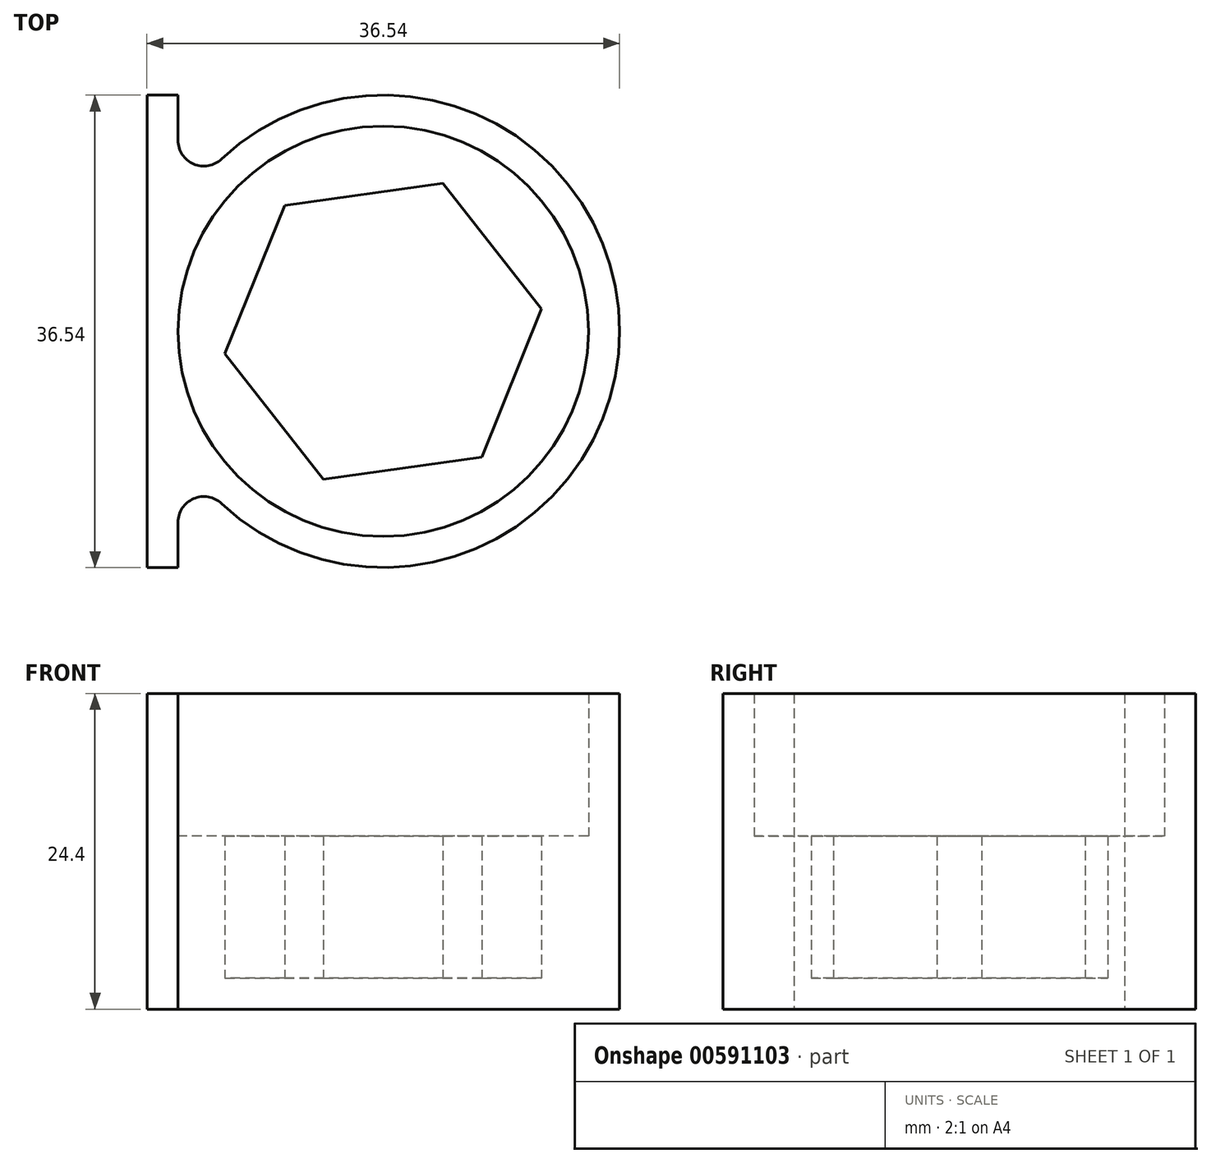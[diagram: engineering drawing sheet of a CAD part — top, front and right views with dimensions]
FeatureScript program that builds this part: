
annotation { "Feature Type Name" : "Feature", "Feature Type Description" : "" }
export const myFeature = defineFeature(function(context is Context, id is Id, definition is map)
    precondition{}
    {
        {
            assignVariable(context, id + "F0", {"name" : "WallThickness", "anyValue" : 2.4 * mm});
        }
        {
            assignVariable(context, id + "F1", {"name" : "HexHeight", "anyValue" : 11 * mm});
        }
        {
            var Q0;
            Q0=qCreatedBy(makeId("Top.planeOp"),FACE);
            var sketch = newSketch(context, id + "F2", { "sketchPlane" : qUnion([Q0])});
            skCircle(sketch, "E0", {"center": v(0, 0) * mm, "radius": 15.86 * mm});
            skCircle(sketch, "E1.cCircle", {"center": v(0, 0) * mm, "radius": 10.7 * mm, "construction": true});
            skLineSegment(sketch, "E1.0", {"start": v(4.62, 11.46) * mm, "end": v(12.23, 1.73) * mm});
            skLineSegment(sketch, "E1.1", {"start": v(12.23, 1.73) * mm, "end": v(7.61, -9.73) * mm});
            skLineSegment(sketch, "E1.2", {"start": v(7.61, -9.73) * mm, "end": v(-4.62, -11.46) * mm});
            skLineSegment(sketch, "E1.3", {"start": v(-4.62, -11.46) * mm, "end": v(-12.23, -1.73) * mm});
            skLineSegment(sketch, "E1.4", {"start": v(-12.23, -1.73) * mm, "end": v(-7.61, 9.73) * mm});
            skLineSegment(sketch, "E1.5", {"start": v(-7.61, 9.73) * mm, "end": v(4.62, 11.46) * mm});
            skPoint(sketch, "E1.0.midPoint", {"position": v(8.43, 6.6) * mm});
            skCircle(sketch, "E2", {"center": v(0, 0) * mm, "radius": 18.26 * mm});
            skLineSegment(sketch, "E3", {"start": v(17.7, 18.27) * mm, "end": v(-22.17, 18.26) * mm, "construction": true});
            skLineSegment(sketch, "E4", {"start": v(-22.17, -18.26) * mm, "end": v(17.7, -18.26) * mm, "construction": true});
            skLineSegment(sketch, "E5", {"start": v(-15.87, 18.26) * mm, "end": v(-15.86, -18.26) * mm});
            skLineSegment(sketch, "E6", {"start": v(-18.27, 18.26) * mm, "end": v(-18.26, -18.26) * mm});
            skLineSegment(sketch, "E7", {"start": v(-18.27, 18.26) * mm, "end": v(-15.87, 18.26) * mm});
            skLineSegment(sketch, "E8", {"start": v(-18.26, -18.26) * mm, "end": v(-15.86, -18.26) * mm});
            skSolve(sketch);
        }
        {
            var Q0;
            {var subQ0=sQuery(id+"F2.wireOp",EDGE,"E2");var subQ1=makeQuery(id+"F2.imprint","INTERSECT",VERTEX,{"derivedFrom":[subQ0,sQuery(id+"F2.wireOp",EDGE,"E6")]});Q0=makeQuery(id+"F2.imprint","IMPRINT",FACE,{"disambiguationData":[TD([[makeQuery(id+"F2.imprint","IMPRINT",EDGE,{"disambiguationData":[TD([[subQ1,1.0]])],"derivedFrom":subQ0}),1.0]])]});}
            var Q1;
            {var subQ5=sQuery(id+"F2.wireOp",EDGE,"E7");Q1=makeQuery(id+"F2.imprint","IMPRINT",FACE,{"disambiguationData":[TD([[makeQuery(id+"F2.imprint","IMPRINT",EDGE,{"derivedFrom":subQ5}),-1.0]])]});}
            var Q2;
            {var subQ5=sQuery(id+"F2.wireOp",EDGE,"E8");Q2=makeQuery(id+"F2.imprint","IMPRINT",FACE,{"disambiguationData":[TD([[makeQuery(id+"F2.imprint","IMPRINT",EDGE,{"derivedFrom":subQ5}),1.0]])]});}
            var Q3;
            {var subQ0=sQuery(id+"F2.wireOp",EDGE,"E0");Q3=makeQuery(id+"F2.imprint","IMPRINT",FACE,{"disambiguationData":[TD([[makeQuery(id+"F2.imprint","IMPRINT",EDGE,{"derivedFrom":subQ0}),-1.0]])]});}
            extrude(context, id + "F3", {"entities" : qUnion([Q0, Q1, Q2, Q3]), "depth" : 22 * mm + getVariable(context, 'WallThickness'), "offsetDistance" : 25 * mm});
        }
        {
            var Q0;
            Q0=makeQuery(id+"F2.imprint","IMPRINT",FACE,{"disambiguationData":[TD([[makeQuery(id+"F2.imprint","IMPRINT",EDGE,{"derivedFrom":sQuery(id+"F2.wireOp",EDGE,"E1.0")}),-1.0]])]});
            var Q1;
            Q1=makeQuery(id+"F2.imprint","IMPRINT",FACE,{"disambiguationData":[TD([[makeQuery(id+"F2.imprint","IMPRINT",EDGE,{"derivedFrom":sQuery(id+"F2.wireOp",EDGE,"E0")}),1.0]])]});
            var Q2;
            {var subQ0=sQuery(id+"F2.wireOp",EDGE,"E0");Q2=makeQuery(id+"F2.imprint","IMPRINT",FACE,{"disambiguationData":[TD([[makeQuery(id+"F2.imprint","IMPRINT",EDGE,{"derivedFrom":subQ0}),-1.0]])]});}
            extrude(context, id + "F4", {"entities" : qUnion([Q0, Q1, Q2]), "operationType" : NewBodyOperationType.ADD, "depth" : getVariable(context, 'WallThickness'), "offsetDistance" : 25 * mm});
        }
        {
            var Q0;
            Q0=makeQuery(id+"F2.imprint","IMPRINT",FACE,{"disambiguationData":[TD([[makeQuery(id+"F2.imprint","IMPRINT",EDGE,{"derivedFrom":sQuery(id+"F2.wireOp",EDGE,"E0")}),1.0]])]});
            extrude(context, id + "F5", {"entities" : qUnion([Q0]), "operationType" : NewBodyOperationType.ADD, "depth" : getVariable(context, 'HexHeight') + getVariable(context, 'WallThickness'), "offsetDistance" : 25 * mm});
        }
        {
            var Q0;
            {var subQ0=sQuery(id+"F2.wireOp",EDGE,"E5");var subQ1=sQuery(id+"F2.wireOp",EDGE,"E2");Q0=makeQuery(id+"F3.opExtrude","SWEPT_EDGE",EDGE,{"disambiguationData":[OSD([subQ1,subQ0]),TDD([makeQuery(id+"F2.imprint","INTERSECT",VERTEX,{"disambiguationData":[OD(1.0)],"derivedFrom":[subQ1,subQ0]})])]});}
            var Q1;
            {var subQ0=sQuery(id+"F2.wireOp",EDGE,"E5");var subQ1=sQuery(id+"F2.wireOp",EDGE,"E2");Q1=makeQuery(id+"F3.opExtrude","SWEPT_EDGE",EDGE,{"disambiguationData":[OSD([subQ1,subQ0]),TDD([makeQuery(id+"F2.imprint","INTERSECT",VERTEX,{"disambiguationData":[OD(0.0)],"derivedFrom":[subQ1,subQ0]})])]});}
            fillet(context, id + "F6", {"entities" : qUnion([Q0, Q1]), "radius" : 2 * mm, "tangentPropagation" : true, "allowEdgeOverflow" : false});
        }
    });
